# Revit family: PRD_FrankeWS_JntrlUnits_SiriusMultiPurposeSink_SIRX754,SIRX755,SIRX756
name_source: partatom
category: Plumbing Fixtures
revit_build: Autodesk Revit 2018 (Build: 20190510_1515(x64)
units: mm (PartAtom-declared; Revit-internal decimal feet)

## family parameters
Always vertical = Yes
Cut with Voids When Loaded = No
OmniClass Number = 23.45.05.14.14
OmniClass Title = Sinks/Lavatories
Part Type = Normal
Room Calculation Point = No
Round Connector Dimension = Use Diameter
Shared = No
Work Plane-Based = No

## types (3) — shared parameters
AssetType = Fixed
Category = Pr_40_20_96_44, Janitorial sinks
Color = Stainless steel
DrainSize = DN-40-1-1-2INH
DurationUnit = year
Finish = Satin finished
FinishAndMaterial = Stainless steel 1.4301
Form = Stainless steel multi purpose sink
IfcExportAs = IfcSanitaryTerminalType
IfcExportType = SINK
Manufacturer = KWC Group AG
ManufacturerName = KWC Group AG
ManufacturerURL = www.kwc.com
Material = Stainless steel
NBSDescription = Janitorial units
NBSReference = 45-35-70/401
NominalDepth = 600 mm
NominalHeight = 800 mm  [stored 2.62467 ft]
ProductInformation = https://pim.kwc.com
Shape = Rectangular
SinkMaterial = PRD_AR_StainlessSteel_SatinFinished
SinkMounting = Pedestal
SinkType = Other
URL = www.kwc.com
Uniclass2015Code = Pr_40_20_96_44
Uniclass2015Title = Janitorial sinks
Uniclass2015Version = Products v1.5
Version = 1
WarrantyDurationUnit = year
WaterSupplyOverflowAndWasteHolesOverflow = Yes
WaterSupplyOverflowAndWasteHolesWaste = Center-Center
WaterSupplyOverflowAndWasteHolesWaterSupply = No tapholes
zero-valued in all types: NominalLength

## per-type parameters (varying)
| type | BIMObjectName | Description | Features | GrossWeight | ModelNumber | Name | NetWeight | NominalWidth | Size | WasteSize |
| SIRX754 | PRD_AR_JanitorialUnits_SiriusMultiPurposeSink_SIRX754 | Workroom sink, stainless steel, surface satin finished, material thickness 1.2 mm, base drainage hole with waste body and sludge trap bucket in stainless steel welded on, overflow DN 40 and outlet spigot DN 15, waste set with ball stop valve DN 40 and DN 15, with stainless steel square tube base frame, height adjustable. width: 1000 mm | stainless steel, 1.20 mm, satin finished, no mounting, 1000x800x600 mm (WxHxD) | 51.00 kg | 2000100360 | Sirius multi purpose sink SIRX754 | 26.00 kg | 1000 mm  [stored 3.28084 ft] | 1000 x 600 x 800 mm | 40  [stored 0.131234 ft] |
| SIRX755 | PRD_AR_JanitorialUnits_SiriusMultiPurposeSink_SIRX755 | Workroom sink, stainless steel, surface satin finished, material thickness 1.2 mm, base drainage hole with waste body and sludge trap bucket in stainless steel welded on, overflow DN 40 and outlet spigot DN 15, waste set with ball stop valve DN 40 and DN 15, with stainless steel square tube base frame, height adjustable. width: 1500 mm | stainless steel, 1.20 mm, satin finished, no mounting, 1500x800x600 mm (WxHxD) | 58.40 kg | 2000100361 | Sirius multi purpose sink SIRX755 | 32.00 kg | 1500 mm  [stored 4.92126 ft] | 1500 x 600 x 800 mm | 38.1  [stored 0.125 ft] |
| SIRX756 | PRD_AR_JanitorialUnits_SiriusMultiPurposeSink_SIRX756 | Workroom sink, stainless steel, surface satin finished, material thickness 1.2 mm, base drainage hole with waste body and sludge trap bucket in stainless steel welded on, overflow DN 40 and outlet spigot DN 15, waste set with ball stop valve DN 40 and DN 15, with stainless steel square tube base frame, height adjustable. width: 2000 mm | stainless steel, 1.20 mm, satin finished, no mounting, 2000x800x600 mm (WxHxD) | 72.80 kg | 2000100362 | Sirius multi purpose sink SIRX756 | 42.00 kg | 2000 mm  [stored 6.56168 ft] | 2000 x 600 x 800 mm | 38.1  [stored 0.125 ft] |

note: column(s) folded — value = type name in every type: Model, ModelReference

note: [stored X ft] marks values corroborated as IEEE doubles in the binary element streams (Revit-internal decimal feet)

## geometry (parser evidence)
native form markers: Sweep x5
no freeform markers — native parametric forms only
